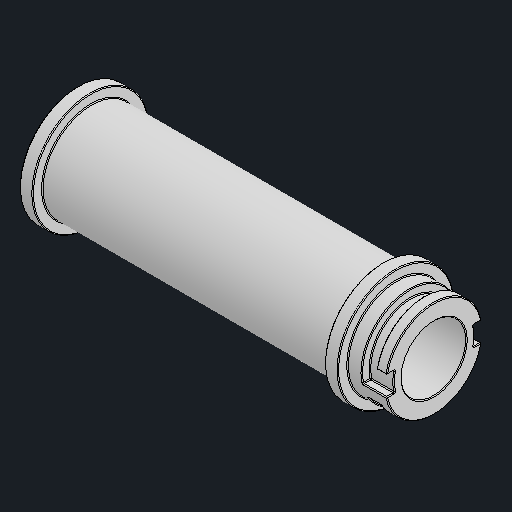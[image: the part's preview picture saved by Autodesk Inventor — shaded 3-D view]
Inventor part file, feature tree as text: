
AUTODESK INVENTOR PART (.ipt)
format: ipt  version: 2024.2 (Build 282272000, 272)  size: 347,648 bytes
history: native  units: mm
features: other x1, fillet x1
ambient origin geometry x8: Origin, YZ Plane, XZ Plane, XY Plane, X Axis, Y Axis, Z Axis, Center Point
bodies: Body1 (feature_tree)
feature tree (2):
  other  "솔리드1"
  fillet  "Fillet4"  [1 undecoded]
note: 1 required parameter value undecoded (feature->parameter linkage not recoverable at this tier; creation-order binding heuristic only, values carry confidence <= 0.55)
